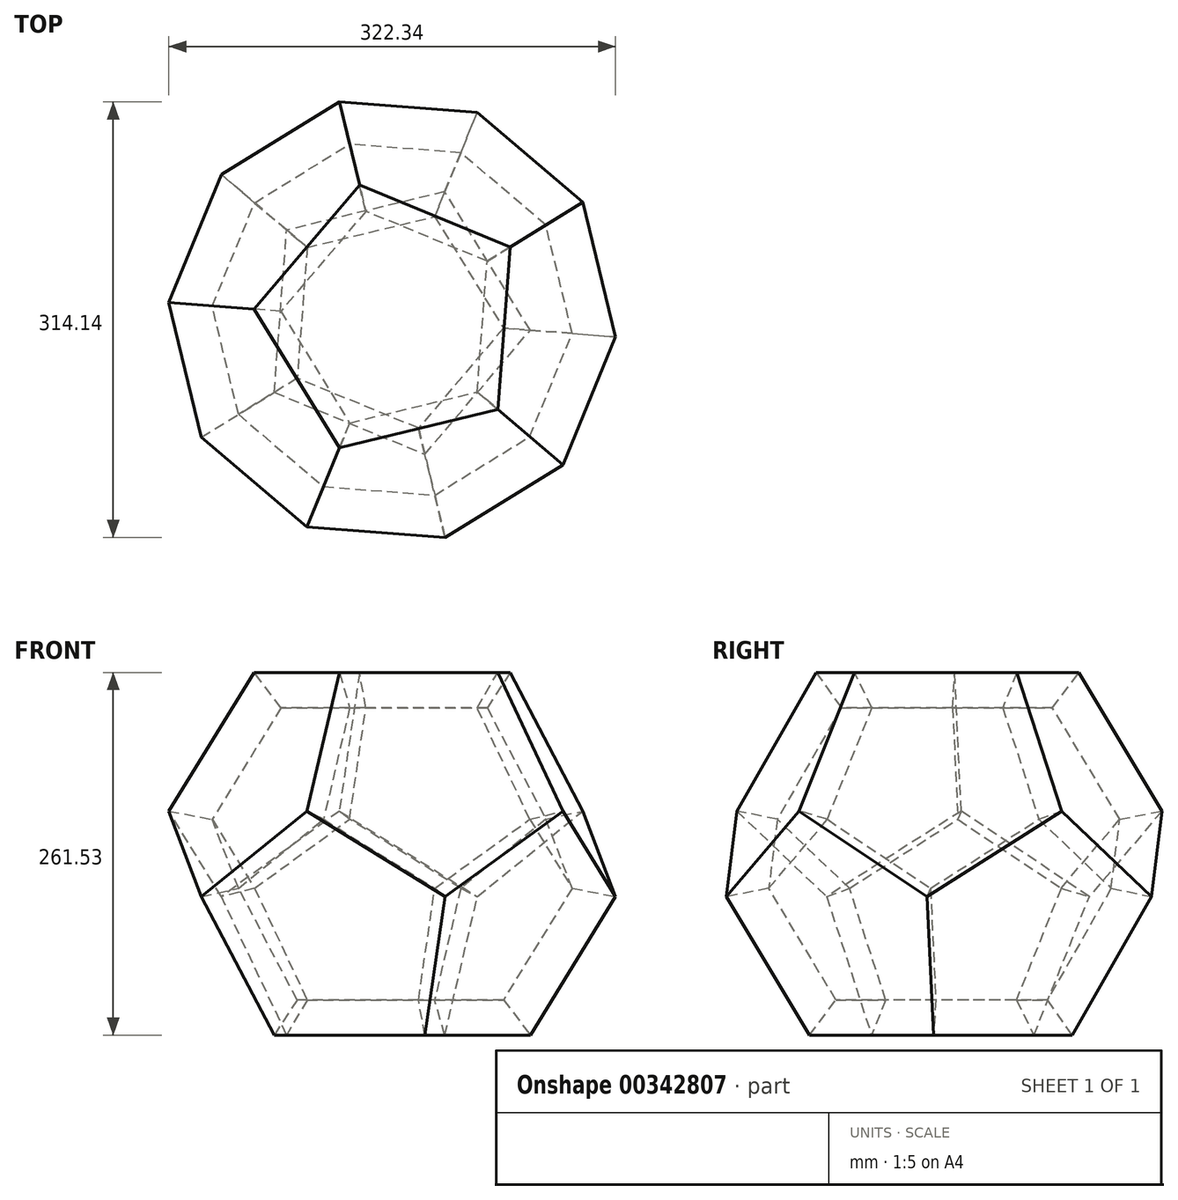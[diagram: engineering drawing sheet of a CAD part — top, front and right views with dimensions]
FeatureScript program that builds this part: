
annotation { "Feature Type Name" : "Feature", "Feature Type Description" : "" }
export const myFeature = defineFeature(function(context is Context, id is Id, definition is map)
    precondition{}
    {
        {
            var Q0;
            Q0=qCreatedBy(makeId("Top.planeOp"),FACE);
            var sketch = newSketch(context, id + "F0", { "sketchPlane" : qUnion([Q0])});
            skCircle(sketch, "E0.cCircle", {"center": v(0, 0) * mm, "radius": 80.82 * mm, "construction": true});
            skLineSegment(sketch, "E0.0", {"start": v(99.6, -7.58) * mm, "end": v(23.57, -97.07) * mm});
            skLineSegment(sketch, "E0.1", {"start": v(23.57, -97.07) * mm, "end": v(-85.04, -52.42) * mm});
            skLineSegment(sketch, "E0.2", {"start": v(-85.04, -52.42) * mm, "end": v(-76.13, 64.68) * mm});
            skLineSegment(sketch, "E0.3", {"start": v(-76.13, 64.68) * mm, "end": v(37.99, 92.39) * mm});
            skLineSegment(sketch, "E0.4", {"start": v(37.99, 92.39) * mm, "end": v(99.6, -7.58) * mm});
            skPoint(sketch, "E0.0.midPoint", {"position": v(61.59, -52.33) * mm});
            skSolve(sketch);
        }
        {
            var Q0;
            Q0=makeQuery(id+"F0.imprint","IMPRINT",FACE,{"disambiguationData":[TD([[makeQuery(id+"F0.imprint","IMPRINT",EDGE,{"derivedFrom":sQuery(id+"F0.wireOp",EDGE,"E0.0")}),-1.0]])]});
            extrude(context, id + "F1", {"entities" : qUnion([Q0]), "depth" : 25.4 * mm});
        }
        {
            var Q0;
            Q0=makeQuery(id+"F1.opExtrude","CAP_EDGE",EDGE,{"disambiguationData":[OSD([sQuery(id+"F0.wireOp",EDGE,"E0.1")])],"isStart":false});
            var Q1;
            Q1=makeQuery(id+"F1.opExtrude","CAP_EDGE",EDGE,{"disambiguationData":[OSD([sQuery(id+"F0.wireOp",EDGE,"E0.2")])],"isStart":false});
            var Q2;
            Q2=makeQuery(id+"F1.opExtrude","CAP_EDGE",EDGE,{"disambiguationData":[OSD([sQuery(id+"F0.wireOp",EDGE,"E0.3")])],"isStart":false});
            var Q3;
            Q3=makeQuery(id+"F1.opExtrude","CAP_EDGE",EDGE,{"disambiguationData":[OSD([sQuery(id+"F0.wireOp",EDGE,"E0.4")])],"isStart":false});
            var Q4;
            Q4=makeQuery(id+"F1.opExtrude","CAP_EDGE",EDGE,{"disambiguationData":[OSD([sQuery(id+"F0.wireOp",EDGE,"E0.0")])],"isStart":false});
            chamfer(context, id + "F2", {"entities" : qUnion([Q0, Q1, Q2, Q3, Q4]), "chamferType" : ChamferType.OFFSET_ANGLE, "width" : 25.4 * mm, "oppositeDirection" : false, "angle" : 31.72 * degree, "tangentPropagation" : true});
        }
        {
            var Q0;
            Q0=makeQuery(id+"F1.opExtrude","SWEPT_BODY",BODY,{"disambiguationData":[OSD([sQuery(id+"F0.wireOp",EDGE,"E0.0"),sQuery(id+"F0.wireOp",EDGE,"E0.1"),sQuery(id+"F0.wireOp",EDGE,"E0.2"),sQuery(id+"F0.wireOp",EDGE,"E0.3"),sQuery(id+"F0.wireOp",EDGE,"E0.4")])]});
            var Q1;
            Q1=makeQuery(id+"F2.opChamfer","BLEND_EDGE",EDGE,{"blendedFrom":[makeQuery(id+"F1.opExtrude","CAP_EDGE",EDGE,{"disambiguationData":[OSD([sQuery(id+"F0.wireOp",EDGE,"E0.1")])],"isStart":false}),makeQuery(id+"F1.opExtrude","CAP_EDGE",EDGE,{"disambiguationData":[OSD([sQuery(id+"F0.wireOp",EDGE,"E0.2")])],"isStart":false})],"blendedInto":[]});
            circularPattern(context, id + "F3", {"entities" : qUnion([Q0]), "axis" : qUnion([Q1]), "angle" : 360 * degree, "instanceCount" : 3, "equalSpace" : true});
        }
        {
            var Q0;
            Q0=makeQuery(id+"F1.opExtrude","SWEPT_BODY",BODY,{"disambiguationData":[OSD([sQuery(id+"F0.wireOp",EDGE,"E0.0"),sQuery(id+"F0.wireOp",EDGE,"E0.1"),sQuery(id+"F0.wireOp",EDGE,"E0.2"),sQuery(id+"F0.wireOp",EDGE,"E0.3"),sQuery(id+"F0.wireOp",EDGE,"E0.4")])]});
            var Q1;
            Q1=makeQuery(id+"F3.opPattern","COPY",BODY,{"derivedFrom":makeQuery(id+"F1.opExtrude","SWEPT_BODY",BODY,{"disambiguationData":[OSD([sQuery(id+"F0.wireOp",EDGE,"E0.0"),sQuery(id+"F0.wireOp",EDGE,"E0.1"),sQuery(id+"F0.wireOp",EDGE,"E0.2"),sQuery(id+"F0.wireOp",EDGE,"E0.3"),sQuery(id+"F0.wireOp",EDGE,"E0.4")])]}),"instanceName":"1"});
            var Q2;
            Q2=makeQuery(id+"F3.opPattern","COPY",BODY,{"derivedFrom":makeQuery(id+"F1.opExtrude","SWEPT_BODY",BODY,{"disambiguationData":[OSD([sQuery(id+"F0.wireOp",EDGE,"E0.0"),sQuery(id+"F0.wireOp",EDGE,"E0.1"),sQuery(id+"F0.wireOp",EDGE,"E0.2"),sQuery(id+"F0.wireOp",EDGE,"E0.3"),sQuery(id+"F0.wireOp",EDGE,"E0.4")])]}),"instanceName":"2"});
            var Q3;
            Q3=makeQuery(id+"F2.opChamfer","BLEND_EDGE",EDGE,{"blendedFrom":[makeQuery(id+"F1.opExtrude","CAP_EDGE",EDGE,{"disambiguationData":[OSD([sQuery(id+"F0.wireOp",EDGE,"E0.0")])],"isStart":false}),makeQuery(id+"F1.opExtrude","CAP_EDGE",EDGE,{"disambiguationData":[OSD([sQuery(id+"F0.wireOp",EDGE,"E0.4")])],"isStart":false})],"blendedInto":[]});
            transform(context, id + "F4", {"entities" : qUnion([Q0, Q1, Q2]), "transformType" : TransformType.ROTATION, "transformAxis" : qUnion([Q3]), "angle" : 120 * degree, "makeCopy" : true});
        }
        {
            var Q0;
            Q0=makeQuery(id+"F4.opPattern","COPY",BODY,{"derivedFrom":makeQuery(id+"F3.opPattern","COPY",BODY,{"derivedFrom":makeQuery(id+"F1.opExtrude","SWEPT_BODY",BODY,{"disambiguationData":[OSD([sQuery(id+"F0.wireOp",EDGE,"E0.0"),sQuery(id+"F0.wireOp",EDGE,"E0.1"),sQuery(id+"F0.wireOp",EDGE,"E0.2"),sQuery(id+"F0.wireOp",EDGE,"E0.3"),sQuery(id+"F0.wireOp",EDGE,"E0.4")])]}),"instanceName":"1"}),"instanceName":"1"});
            var Q1;
            Q1=makeQuery(id+"F4.opPattern","COPY",BODY,{"derivedFrom":makeQuery(id+"F3.opPattern","COPY",BODY,{"derivedFrom":makeQuery(id+"F1.opExtrude","SWEPT_BODY",BODY,{"disambiguationData":[OSD([sQuery(id+"F0.wireOp",EDGE,"E0.0"),sQuery(id+"F0.wireOp",EDGE,"E0.1"),sQuery(id+"F0.wireOp",EDGE,"E0.2"),sQuery(id+"F0.wireOp",EDGE,"E0.3"),sQuery(id+"F0.wireOp",EDGE,"E0.4")])]}),"instanceName":"2"}),"instanceName":"1"});
            var Q2;
            Q2=makeQuery(id+"F4.opPattern","COPY",BODY,{"derivedFrom":makeQuery(id+"F1.opExtrude","SWEPT_BODY",BODY,{"disambiguationData":[OSD([sQuery(id+"F0.wireOp",EDGE,"E0.0"),sQuery(id+"F0.wireOp",EDGE,"E0.1"),sQuery(id+"F0.wireOp",EDGE,"E0.2"),sQuery(id+"F0.wireOp",EDGE,"E0.3"),sQuery(id+"F0.wireOp",EDGE,"E0.4")])]}),"instanceName":"1"});
            var Q3;
            Q3=makeQuery(id+"F4.opPattern","COPY",EDGE,{"derivedFrom":makeQuery(id+"F3.opPattern","COPY",EDGE,{"derivedFrom":makeQuery(id+"F2.opChamfer","BLEND_EDGE",EDGE,{"blendedFrom":[makeQuery(id+"F1.opExtrude","CAP_EDGE",EDGE,{"disambiguationData":[OSD([sQuery(id+"F0.wireOp",EDGE,"E0.0")])],"isStart":false}),makeQuery(id+"F1.opExtrude","CAP_EDGE",EDGE,{"disambiguationData":[OSD([sQuery(id+"F0.wireOp",EDGE,"E0.4")])],"isStart":false})],"blendedInto":[]}),"instanceName":"2"}),"instanceName":"1"});
            transform(context, id + "F5", {"entities" : qUnion([Q0, Q1, Q2]), "transformType" : TransformType.ROTATION, "transformAxis" : qUnion([Q3]), "angle" : 120 * degree, "makeCopy" : true});
        }
        {
            var Q0;
            Q0=makeQuery(id+"F5.opPattern","COPY",BODY,{"derivedFrom":makeQuery(id+"F4.opPattern","COPY",BODY,{"derivedFrom":makeQuery(id+"F1.opExtrude","SWEPT_BODY",BODY,{"disambiguationData":[OSD([sQuery(id+"F0.wireOp",EDGE,"E0.0"),sQuery(id+"F0.wireOp",EDGE,"E0.1"),sQuery(id+"F0.wireOp",EDGE,"E0.2"),sQuery(id+"F0.wireOp",EDGE,"E0.3"),sQuery(id+"F0.wireOp",EDGE,"E0.4")])]}),"instanceName":"1"}),"instanceName":"1"});
            var Q1;
            Q1=makeQuery(id+"F4.opPattern","COPY",BODY,{"derivedFrom":makeQuery(id+"F3.opPattern","COPY",BODY,{"derivedFrom":makeQuery(id+"F1.opExtrude","SWEPT_BODY",BODY,{"disambiguationData":[OSD([sQuery(id+"F0.wireOp",EDGE,"E0.0"),sQuery(id+"F0.wireOp",EDGE,"E0.1"),sQuery(id+"F0.wireOp",EDGE,"E0.2"),sQuery(id+"F0.wireOp",EDGE,"E0.3"),sQuery(id+"F0.wireOp",EDGE,"E0.4")])]}),"instanceName":"2"}),"instanceName":"1"});
            var Q2;
            Q2=makeQuery(id+"F5.opPattern","COPY",BODY,{"derivedFrom":makeQuery(id+"F4.opPattern","COPY",BODY,{"derivedFrom":makeQuery(id+"F3.opPattern","COPY",BODY,{"derivedFrom":makeQuery(id+"F1.opExtrude","SWEPT_BODY",BODY,{"disambiguationData":[OSD([sQuery(id+"F0.wireOp",EDGE,"E0.0"),sQuery(id+"F0.wireOp",EDGE,"E0.1"),sQuery(id+"F0.wireOp",EDGE,"E0.2"),sQuery(id+"F0.wireOp",EDGE,"E0.3"),sQuery(id+"F0.wireOp",EDGE,"E0.4")])]}),"instanceName":"2"}),"instanceName":"1"}),"instanceName":"1"});
            var Q3;
            Q3=makeQuery(id+"F5.opPattern","COPY",EDGE,{"derivedFrom":makeQuery(id+"F4.opPattern","COPY",EDGE,{"derivedFrom":makeQuery(id+"F3.opPattern","COPY",EDGE,{"derivedFrom":makeQuery(id+"F2.opChamfer","BLEND_EDGE",EDGE,{"blendedFrom":[makeQuery(id+"F1.opExtrude","CAP_EDGE",EDGE,{"disambiguationData":[OSD([sQuery(id+"F0.wireOp",EDGE,"E0.2")])],"isStart":false}),makeQuery(id+"F1.opExtrude","CAP_EDGE",EDGE,{"disambiguationData":[OSD([sQuery(id+"F0.wireOp",EDGE,"E0.3")])],"isStart":false})],"blendedInto":[]}),"instanceName":"2"}),"instanceName":"1"}),"instanceName":"1"});
            transform(context, id + "F6", {"entities" : qUnion([Q0, Q1, Q2]), "transformType" : TransformType.ROTATION, "transformAxis" : qUnion([Q3]), "angle" : 240 * degree, "makeCopy" : true});
        }
    });
